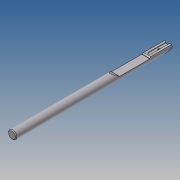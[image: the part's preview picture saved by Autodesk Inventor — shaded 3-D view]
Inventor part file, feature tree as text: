
AUTODESK INVENTOR PART (.ipt)
format: ipt  version: 2018.3 (Build 223284000, 284)  size: 184,320 bytes
history: native  units: in
note: dims shown in document units (in); Inventor stores cm internally (conversion verified against a paired STEP export)
features: sketch x8, extrude x7, chamfer x3, hole x1, revolve x1
ambient origin geometry x8: Origin, YZ Plane, XZ Plane, XY Plane, X Axis, Y Axis, Z Axis, Center Point
bodies: Solid1 (feature_tree)
feature tree (20):
  extrude  "Extrusion1"  Depth=2.9528in TaperAngle=0.0deg
  sketch  "Sketch2"  dims[d6=0.04in d7=0.375in d8=0.0in]
  extrude  "Extrusion3"  Depth=0.375in TaperAngle=0.0deg
  extrude  "Extrusion4"  Depth=0.056in
  hole  "Hole1"  [1 undecoded]
  extrude  "Extrusion5"  TaperAngle=30.0deg  [1 undecoded]
  chamfer  "Chamfer1"  Distance=0.5in
  chamfer  "Chamfer2"  Distance=0.01in Angle=45.0deg
  chamfer  "Chamfer3"  Distance=0.01in Angle=45.0deg
  extrude  "Extrusion7"  Depth=0.018in
  extrude  "Extrusion8"  TaperAngle=0.0deg  [1 undecoded]
  extrude  "Extrusion10"  Depth=0.58in
  sketch  "Sketch12"  dims[d32=0.015in d33=0.015in d34=45.0deg d40=0.018in]
  revolve  "Revolution1"  [1 undecoded]
  sketch  "Sketch1"  dims[d0=0.1575in d1=2.9528in d2=0.0in]
  sketch  "Sketch3"  dims[d9=60.0deg d10=0.056in]
  sketch  "Sketch4"  dims[d11=0.032in d12=0.345in d13=0.0in]
  sketch  "Sketch6"  dims[d14=0.165in]
  sketch  "Sketch11"  dims[d15=0.048in d16=0.126in d17=0.375in d18=0.25in d19=0.5635in d20=0.209in d21=0.8108in d23=30.0deg d24=0.5in d25=0.0in d26=0.01in d27=0.015in d28=45.0deg d29=0.01in d30=0.015in d31=45.0deg]
  sketch  "Sketch14"  dims[d41=1.0in d42=0.0in d43=0.0in d45=0.35in d46=0.02in d47=0.0in d56=0.005in d57=0.42in d58=0.005in d59=30.0deg d61=0.25in d62=0.0in d64=30.0deg d65=0.063in d66=0.0551in d67=90.0deg d68=0.42in d69=0.58in]
note: 4 required parameter values undecoded (feature->parameter linkage not recoverable at this tier; creation-order binding heuristic only, values carry confidence <= 0.55)